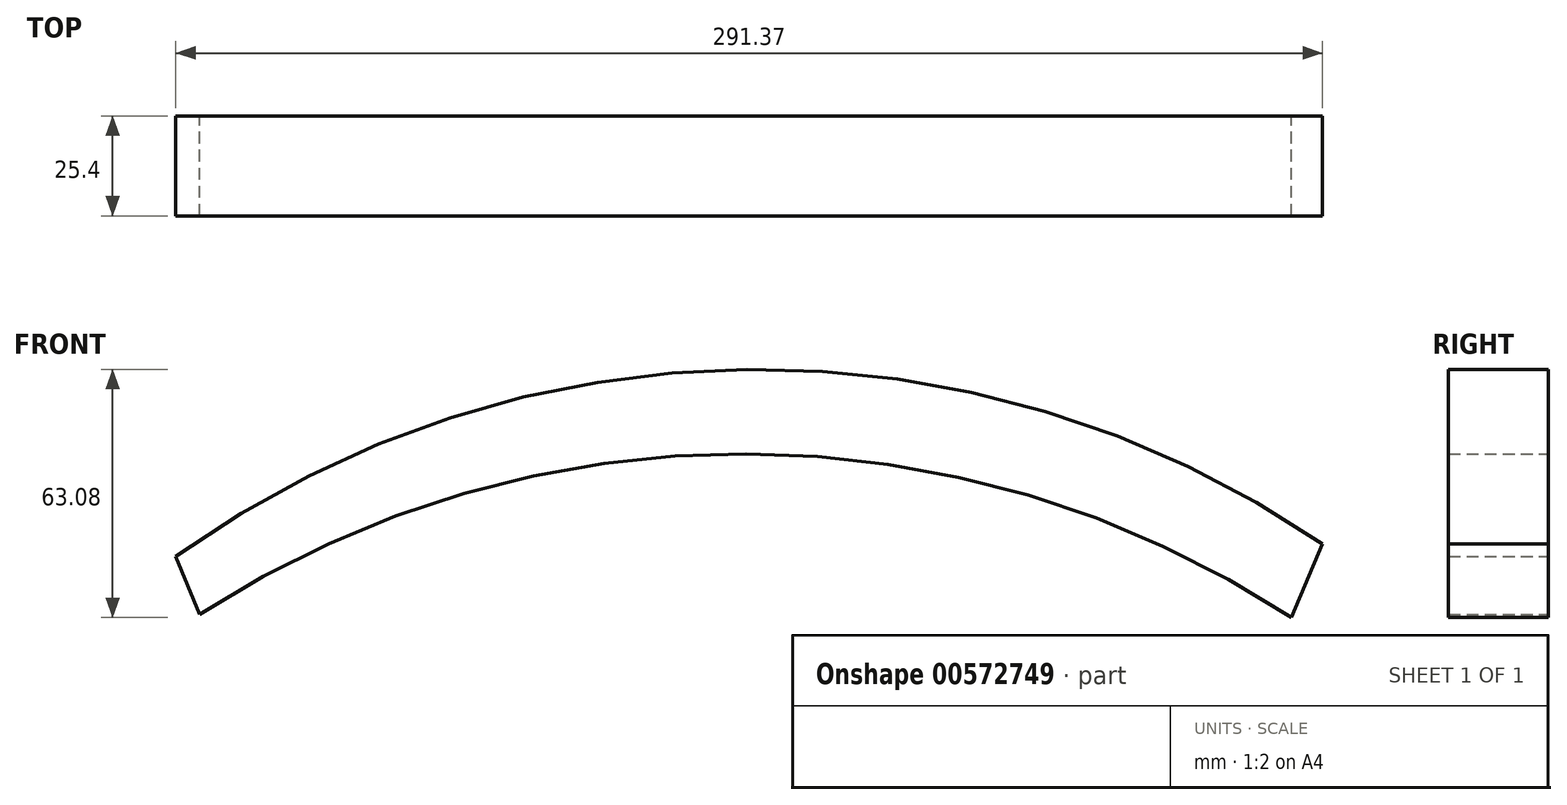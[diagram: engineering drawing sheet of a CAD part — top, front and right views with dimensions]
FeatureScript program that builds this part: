
annotation { "Feature Type Name" : "Feature", "Feature Type Description" : "" }
export const myFeature = defineFeature(function(context is Context, id is Id, definition is map)
    precondition{}
    {
        {
            var Q0;
            Q0=qCreatedBy(makeId("Front.planeOp"),FACE);
            var sketch = newSketch(context, id + "F0", { "sketchPlane" : qUnion([Q0])});
            skArc(sketch, "E0", {"start": v(180.14, 15.47) * mm, "mid": v(33.96, 59.85) * mm, "end": v(-111.23, 12.35) * mm});
            skArc(sketch, "E1", {"start": v(172.24, -3.22) * mm, "mid": v(33.69, 38.4) * mm, "end": v(-105.12, -2.37) * mm});
            skLineSegment(sketch, "E2", {"start": v(-111.23, 12.35) * mm, "end": v(-105.12, -2.37) * mm});
            skLineSegment(sketch, "E3", {"start": v(180.14, 15.47) * mm, "end": v(172.24, -3.22) * mm});
            skSolve(sketch);
        }
        {
            var Q0;
            Q0=makeQuery(id+"F0.imprint","IMPRINT",FACE,{"disambiguationData":[TD([[makeQuery(id+"F0.imprint","IMPRINT",EDGE,{"derivedFrom":sQuery(id+"F0.wireOp",EDGE,"E0")}),1.0]])]});
            extrude(context, id + "F1", {"entities" : qUnion([Q0]), "depth" : 25.4 * mm, "offsetDistance" : 25.4 * mm});
        }
    });
